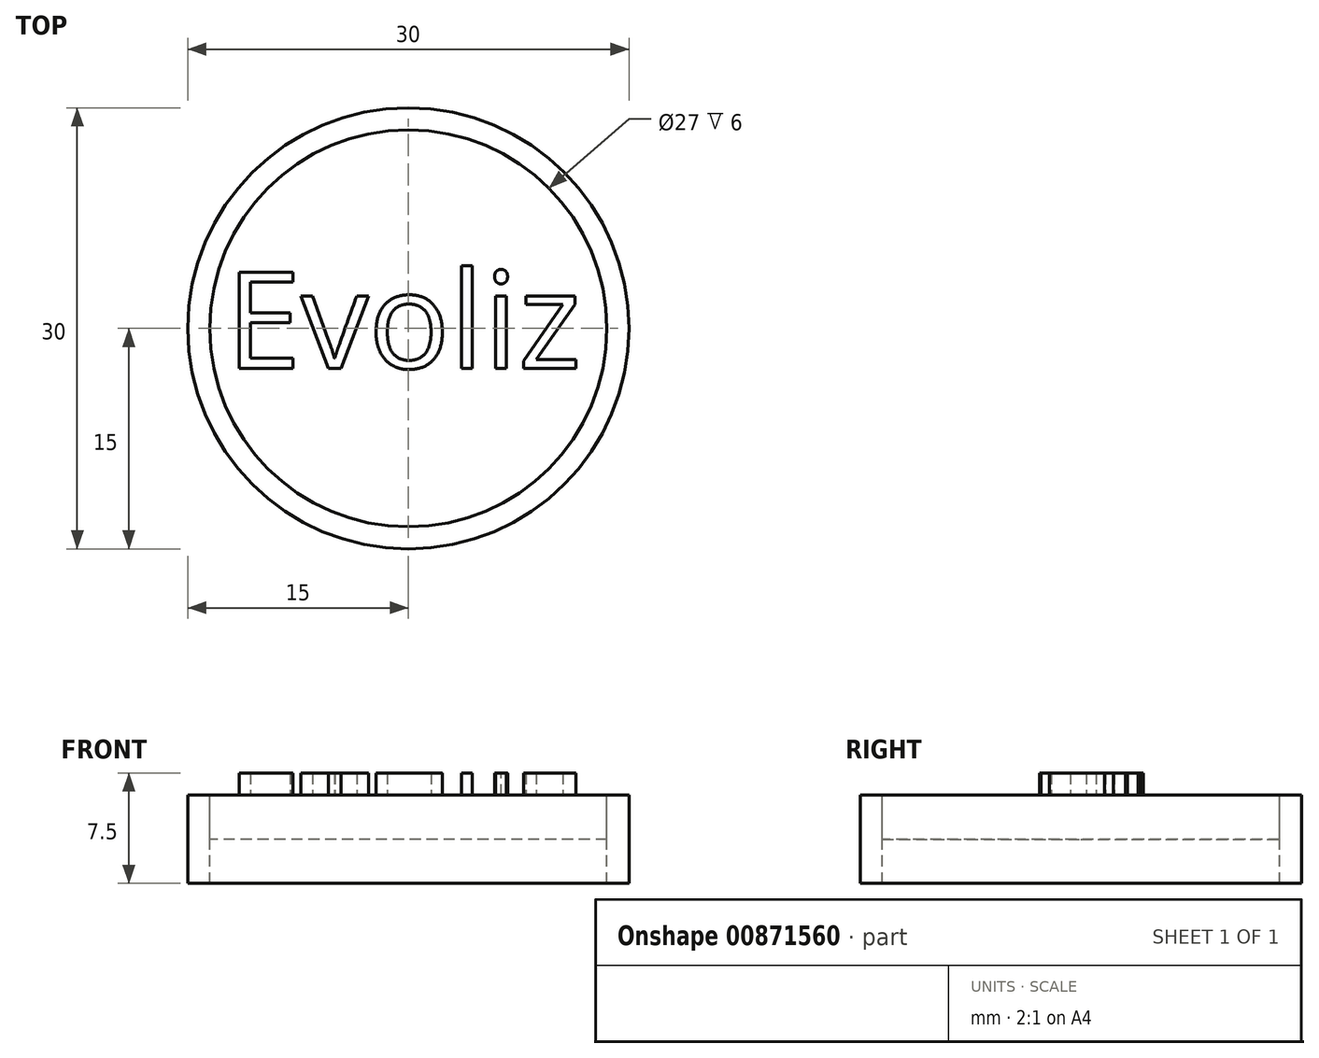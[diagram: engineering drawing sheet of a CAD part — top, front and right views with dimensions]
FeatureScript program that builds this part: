
annotation { "Feature Type Name" : "Feature", "Feature Type Description" : "" }
export const myFeature = defineFeature(function(context is Context, id is Id, definition is map)
    precondition{}
    {
        {
            var Q0;
            Q0=qCreatedBy(makeId("Top.planeOp"),FACE);
            var sketch = newSketch(context, id + "F0", { "sketchPlane" : qUnion([Q0])});
            skCircle(sketch, "E0", {"center": v(0, 0) * mm, "radius": 15 * mm});
            skCircle(sketch, "E1", {"center": v(0, 0) * mm, "radius": 13.5 * mm});
            skSolve(sketch);
        }
        {
            var Q0;
            Q0=makeQuery(id+"F0.imprint","IMPRINT",FACE,{"disambiguationData":[TD([[makeQuery(id+"F0.imprint","IMPRINT",EDGE,{"derivedFrom":sQuery(id+"F0.wireOp",EDGE,"E1")}),1.0]])]});
            extrude(context, id + "F1", {"entities" : qUnion([Q0]), "depth" : -3 * mm, "offsetDistance" : 25 * mm});
        }
        {
            var Q0;
            Q0=makeQuery(id+"F0.imprint","IMPRINT",FACE,{"disambiguationData":[TD([[makeQuery(id+"F0.imprint","IMPRINT",EDGE,{"derivedFrom":sQuery(id+"F0.wireOp",EDGE,"E0")}),1.0]])]});
            extrude(context, id + "F2", {"entities" : qUnion([Q0]), "depth" : -6 * mm, "offsetDistance" : 25 * mm});
        }
        {
            var Q0;
            Q0=makeQuery(id+"F0.imprint","IMPRINT",FACE,{"disambiguationData":[TD([[makeQuery(id+"F0.imprint","IMPRINT",EDGE,{"derivedFrom":sQuery(id+"F0.wireOp",EDGE,"E1")}),1.0]])]});
            var sketch = newSketch(context, id + "F3", { "sketchPlane" : qUnion([Q0])});
            skText(sketch, "E2", { "text": "Evoliz", "fontName": "OpenSans-Regular.ttf"});
            const initialGuessF3  = {"E2": [-0.0124, -0.00271, 1, 0, 0.0066]};
            skSetInitialGuess(sketch, initialGuessF3);
            skSolve(sketch);
        }
        {
            var Q0;
            Q0 = qSketchRegion(id + "F3", true);
            extrude(context, id + "F4", {"entities" : qUnion([Q0]), "operationType" : NewBodyOperationType.ADD, "depth" : 1.5 * mm, "offsetDistance" : 25 * mm});
        }
    });
